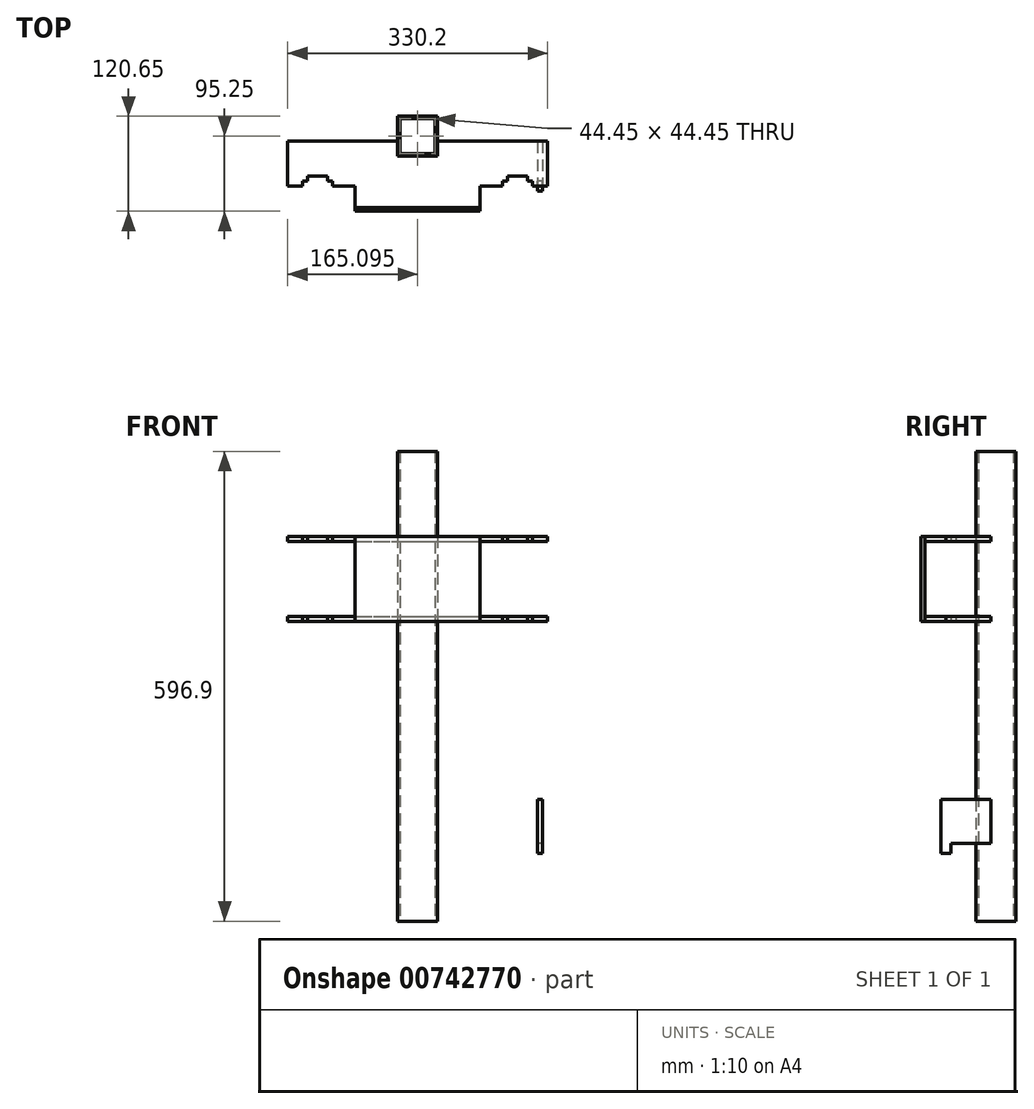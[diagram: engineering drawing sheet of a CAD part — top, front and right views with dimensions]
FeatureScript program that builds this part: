
annotation { "Feature Type Name" : "Feature", "Feature Type Description" : "" }
export const myFeature = defineFeature(function(context is Context, id is Id, definition is map)
    precondition{}
    {
        {
            var Q0;
            Q0=qCreatedBy(makeId("Top.planeOp"),FACE);
            var sketch = newSketch(context, id + "F0", { "sketchPlane" : qUnion([Q0])});
            skLineSegment(sketch, "E0.bottom", {"start": v(-87.24, 0) * mm, "end": v(52.46, 0) * mm});
            skLineSegment(sketch, "E0.top", {"start": v(-87.24, -57.15) * mm, "end": v(-68.2, -57.15) * mm});
            skLineSegment(sketch, "E0.left", {"start": v(-87.24, 0) * mm, "end": v(-87.24, -57.15) * mm});
            skLineSegment(sketch, "E0.right", {"start": v(242.96, 0) * mm, "end": v(242.96, -57.15) * mm});
            skLineSegment(sketch, "E1.top", {"start": v(-68.2, -50.8) * mm, "end": v(-61.84, -50.8) * mm});
            skLineSegment(sketch, "E1.left", {"start": v(-68.2, -57.15) * mm, "end": v(-68.2, -50.8) * mm});
            skLineSegment(sketch, "E1.right", {"start": v(-30.1, -57.15) * mm, "end": v(-30.1, -50.8) * mm});
            skLineSegment(sketch, "E2.bottom", {"start": v(185.8, -50.8) * mm, "end": v(192.16, -50.8) * mm});
            skLineSegment(sketch, "E2.left", {"start": v(185.8, -50.8) * mm, "end": v(185.8, -57.15) * mm});
            skLineSegment(sketch, "E2.right", {"start": v(223.9, -50.8) * mm, "end": v(223.9, -57.15) * mm});
            skLineSegment(sketch, "E3.top", {"start": v(192.16, -44.45) * mm, "end": v(217.56, -44.45) * mm});
            skLineSegment(sketch, "E3.left", {"start": v(192.16, -50.8) * mm, "end": v(192.16, -44.45) * mm});
            skLineSegment(sketch, "E3.right", {"start": v(217.56, -50.8) * mm, "end": v(217.56, -44.45) * mm});
            skLineSegment(sketch, "E4.top", {"start": v(-61.84, -44.45) * mm, "end": v(-36.44, -44.45) * mm});
            skLineSegment(sketch, "E4.left", {"start": v(-61.84, -50.8) * mm, "end": v(-61.84, -44.45) * mm});
            skLineSegment(sketch, "E4.right", {"start": v(-36.44, -50.8) * mm, "end": v(-36.44, -44.45) * mm});
            skLineSegment(sketch, "E5.trimOffspring", {"start": v(-36.44, -50.8) * mm, "end": v(-30.1, -50.8) * mm});
            skLineSegment(sketch, "E6.trimOffspring", {"start": v(-30.1, -57.15) * mm, "end": v(-1.52, -57.15) * mm});
            skLineSegment(sketch, "E7.trimOffspring", {"start": v(217.56, -50.8) * mm, "end": v(223.9, -50.8) * mm});
            skLineSegment(sketch, "E8.trimOffspring", {"start": v(223.9, -57.15) * mm, "end": v(242.96, -57.15) * mm});
            skLineSegment(sketch, "E9.top", {"start": v(52.46, -19.05) * mm, "end": v(103.26, -19.05) * mm});
            skLineSegment(sketch, "E9.left", {"start": v(52.46, 0) * mm, "end": v(52.46, -19.05) * mm});
            skLineSegment(sketch, "E9.right", {"start": v(103.26, 0) * mm, "end": v(103.26, -19.05) * mm});
            skLineSegment(sketch, "E10.trimOffspring", {"start": v(103.26, 0) * mm, "end": v(242.96, 0) * mm});
            skLineSegment(sketch, "E11.top", {"start": v(-1.52, -84.14) * mm, "end": v(157.23, -84.14) * mm});
            skLineSegment(sketch, "E11.left", {"start": v(-1.52, -57.15) * mm, "end": v(-1.52, -84.14) * mm});
            skLineSegment(sketch, "E11.right", {"start": v(157.23, -57.15) * mm, "end": v(157.23, -84.14) * mm});
            skLineSegment(sketch, "E12.trimOffspring", {"start": v(157.23, -57.15) * mm, "end": v(185.8, -57.15) * mm});
            skSolve(sketch);
        }
        {
            var Q0;
            Q0=qSketchRegion(id+"F0",true);
            extrude(context, id + "F1", {"entities" : qUnion([Q0]), "depth" : 6.35 * mm, "offsetDistance" : 25.4 * mm});
        }
        {
            var Q0;
            Q0=makeQuery(id+"F1.opExtrude","SWEPT_BODY",BODY,{"disambiguationData":[OSD([sQuery(id+"F0.wireOp",EDGE,"E0.bottom"),sQuery(id+"F0.wireOp",EDGE,"E0.top"),sQuery(id+"F0.wireOp",EDGE,"E0.left"),sQuery(id+"F0.wireOp",EDGE,"E0.right"),sQuery(id+"F0.wireOp",EDGE,"E1.top"),sQuery(id+"F0.wireOp",EDGE,"E1.left"),sQuery(id+"F0.wireOp",EDGE,"E1.right"),sQuery(id+"F0.wireOp",EDGE,"E2.bottom"),sQuery(id+"F0.wireOp",EDGE,"E2.left"),sQuery(id+"F0.wireOp",EDGE,"E2.right"),sQuery(id+"F0.wireOp",EDGE,"E3.top"),sQuery(id+"F0.wireOp",EDGE,"E3.left"),sQuery(id+"F0.wireOp",EDGE,"E3.right"),sQuery(id+"F0.wireOp",EDGE,"E4.top"),sQuery(id+"F0.wireOp",EDGE,"E4.left"),sQuery(id+"F0.wireOp",EDGE,"E4.right"),sQuery(id+"F0.wireOp",EDGE,"E5.trimOffspring"),sQuery(id+"F0.wireOp",EDGE,"E6.trimOffspring"),sQuery(id+"F0.wireOp",EDGE,"E7.trimOffspring"),sQuery(id+"F0.wireOp",EDGE,"E8.trimOffspring"),sQuery(id+"F0.wireOp",EDGE,"E9.top"),sQuery(id+"F0.wireOp",EDGE,"E9.left"),sQuery(id+"F0.wireOp",EDGE,"E9.right"),sQuery(id+"F0.wireOp",EDGE,"E10.trimOffspring")])]});
            transform(context, id + "F2", {"entities" : qUnion([Q0]), "transformType" : TransformType.TRANSLATION_3D, "dx" : 0 * mm, "dy" : 0 * mm, "dz" : 101.6 * mm, "makeCopy" : true});
        }
        {
            var Q0;
            Q0=qCreatedBy(makeId("Top.planeOp"),FACE);
            var sketch = newSketch(context, id + "F3", { "sketchPlane" : qUnion([Q0])});
            skLineSegment(sketch, "E13.bottom", {"start": v(52.46, 50.8) * mm, "end": v(103.26, 50.8) * mm});
            skLineSegment(sketch, "E13.top", {"start": v(52.46, 0) * mm, "end": v(103.26, 0) * mm});
            skLineSegment(sketch, "E13.left", {"start": v(52.46, 50.8) * mm, "end": v(52.46, 0) * mm});
            skLineSegment(sketch, "E13.right", {"start": v(103.26, 50.8) * mm, "end": v(103.26, 0) * mm});
            skLineSegment(sketch, "E14.0", {"start": v(100.08, 47.63) * mm, "end": v(100.08, 3.18) * mm});
            skLineSegment(sketch, "E14.1", {"start": v(55.63, 47.62) * mm, "end": v(100.08, 47.63) * mm});
            skLineSegment(sketch, "E14.2", {"start": v(55.63, 47.62) * mm, "end": v(55.63, 3.17) * mm});
            skLineSegment(sketch, "E14.3", {"start": v(55.63, 3.17) * mm, "end": v(100.08, 3.18) * mm});
            skSolve(sketch);
        }
        {
            var Q0;
            Q0=qSketchRegion(id+"F3",true);
            extrude(context, id + "F4", {"entities" : qUnion([Q0]), "depth" : 596.9 * mm, "offsetDistance" : 25.4 * mm});
        }
        {
            var Q0;
            Q0=makeQuery(id+"F4.opExtrude","SWEPT_BODY",BODY,{"disambiguationData":[OSD([sQuery(id+"F3.wireOp",EDGE,"E13.bottom"),sQuery(id+"F3.wireOp",EDGE,"E13.top"),sQuery(id+"F3.wireOp",EDGE,"E13.left"),sQuery(id+"F3.wireOp",EDGE,"E13.right"),sQuery(id+"F3.wireOp",EDGE,"E14.0"),sQuery(id+"F3.wireOp",EDGE,"E14.1"),sQuery(id+"F3.wireOp",EDGE,"E14.2"),sQuery(id+"F3.wireOp",EDGE,"E14.3")])]});
            transform(context, id + "F5", {"entities" : qUnion([Q0]), "transformType" : TransformType.TRANSLATION_3D, "dx" : 0 * mm, "dy" : -19.05 * mm, "dz" : -381 * mm, "makeCopy" : false});
        }
        {
            var Q0;
            Q0=makeQuery(id+"F1.opExtrude","SWEPT_FACE",FACE,{"disambiguationData":[OSD([sQuery(id+"F0.wireOp",EDGE,"E11.top")])]});
            var sketch = newSketch(context, id + "F6", { "sketchPlane" : qUnion([Q0])});
            skLineSegment(sketch, "E15.bottom", {"start": v(-1.52, 107.95) * mm, "end": v(157.23, 107.95) * mm});
            skLineSegment(sketch, "E15.top", {"start": v(-1.52, 0) * mm, "end": v(157.23, 0) * mm});
            skLineSegment(sketch, "E15.left", {"start": v(-1.52, 107.95) * mm, "end": v(-1.52, 0) * mm});
            skLineSegment(sketch, "E15.right", {"start": v(157.23, 107.95) * mm, "end": v(157.23, 0) * mm});
            skSolve(sketch);
        }
        {
            var Q0;
            Q0=qSketchRegion(id+"F6",true);
            extrude(context, id + "F7", {"entities" : qUnion([Q0]), "depth" : 4.76 * mm, "offsetDistance" : 25.4 * mm});
        }
        {
            var Q0;
            Q0=makeQuery(id+"F4.opExtrude","SWEPT_FACE",FACE,{"disambiguationData":[OSD([sQuery(id+"F3.wireOp",EDGE,"E13.right")])]});
            cPlane(context, id + "F8", {"entities" : qUnion([Q0]), "cplaneType" : CPlaneType.OFFSET, "offset" : 127 * mm, "width" : 152.4 * mm, "height" : 152.4 * mm});
        }
        {
            var Q0;
            Q0=qCreatedBy(id+"F8.planeOp",FACE);
            var sketch = newSketch(context, id + "F9", { "sketchPlane" : qUnion([Q0])});
            skLineSegment(sketch, "E16.bottom", {"start": v(0, -282.1) * mm, "end": v(-50.8, -282.1) * mm});
            skLineSegment(sketch, "E16.top", {"start": v(0, -226.48) * mm, "end": v(-63.5, -226.48) * mm});
            skLineSegment(sketch, "E16.left", {"start": v(0, -282.1) * mm, "end": v(0, -226.48) * mm});
            skLineSegment(sketch, "E16.right", {"start": v(-63.5, -294.8) * mm, "end": v(-63.5, -226.48) * mm});
            skLineSegment(sketch, "E17.top", {"start": v(-63.5, -294.8) * mm, "end": v(-50.8, -294.8) * mm});
            skLineSegment(sketch, "E17.right", {"start": v(-50.8, -282.1) * mm, "end": v(-50.8, -294.8) * mm});
            skSolve(sketch);
        }
        {
            var Q0;
            Q0=makeQuery(id+"F9.imprint","IMPRINT",FACE,{"disambiguationData":[TD([[makeQuery(id+"F9.imprint","IMPRINT",EDGE,{"derivedFrom":sQuery(id+"F9.wireOp",EDGE,"E16.bottom")}),-1.0]])]});
            extrude(context, id + "F10", {"entities" : qUnion([Q0]), "depth" : 6.35 * mm, "offsetDistance" : 25.4 * mm});
        }
    });
